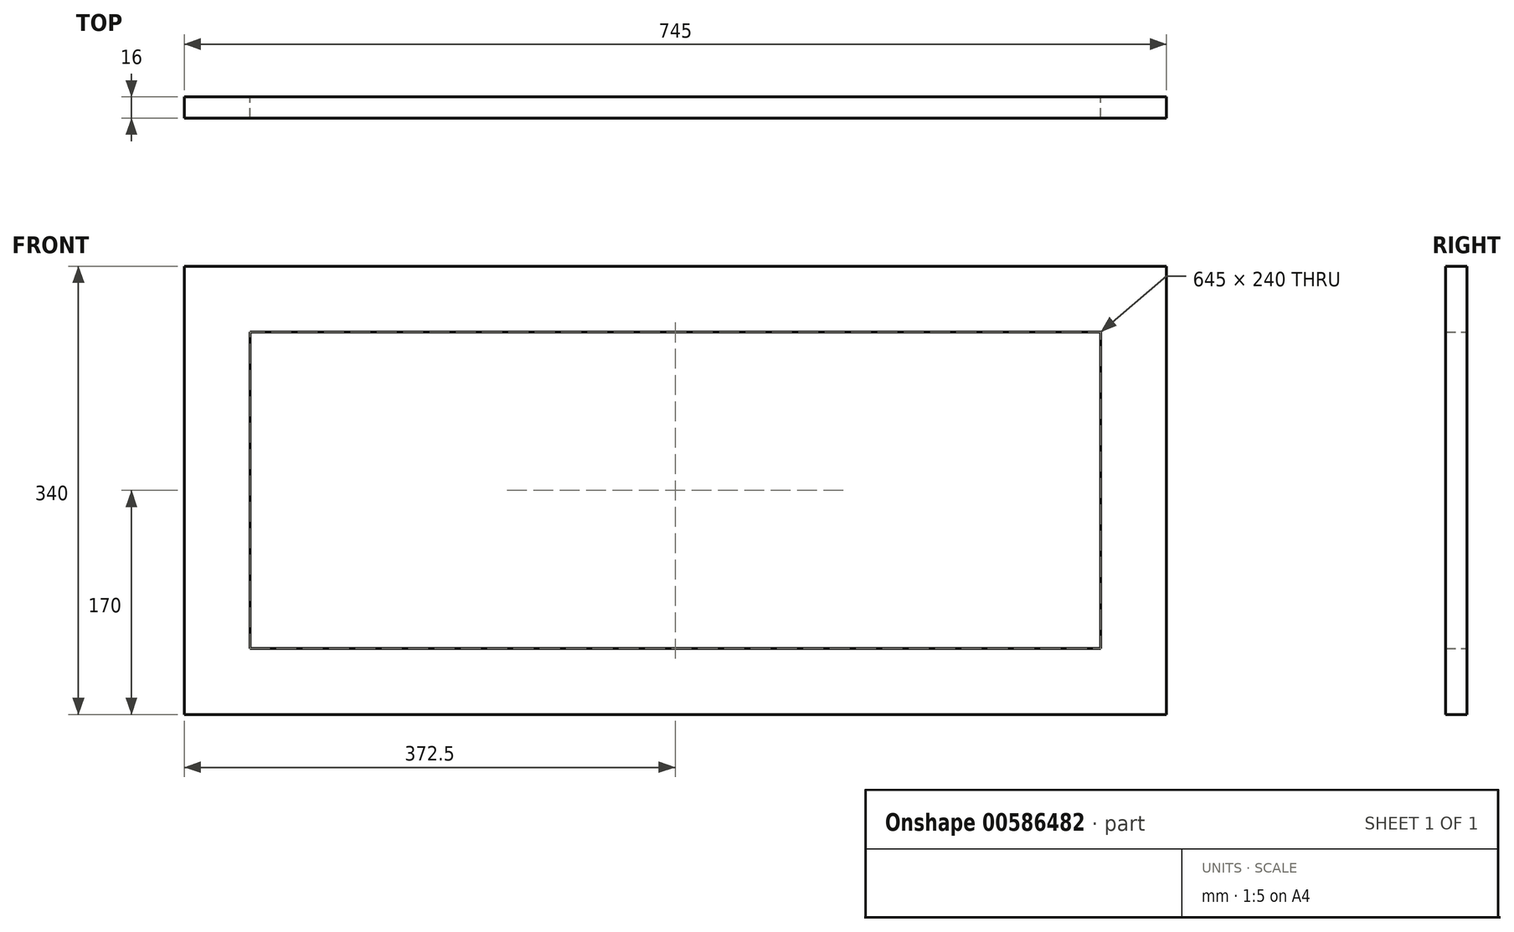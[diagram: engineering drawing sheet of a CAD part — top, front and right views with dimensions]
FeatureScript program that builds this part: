
annotation { "Feature Type Name" : "Feature", "Feature Type Description" : "" }
export const myFeature = defineFeature(function(context is Context, id is Id, definition is map)
    precondition{}
    {
        {
            var Q0;
            Q0=qCreatedBy(makeId("Front.planeOp"),FACE);
            var sketch = newSketch(context, id + "F0", { "sketchPlane" : qUnion([Q0])});
            skLineSegment(sketch, "E0.bottom", {"start": v(-372.5, 170) * mm, "end": v(372.5, 170) * mm});
            skLineSegment(sketch, "E0.top", {"start": v(-372.5, -170) * mm, "end": v(372.5, -170) * mm});
            skLineSegment(sketch, "E0.left", {"start": v(-372.5, 170) * mm, "end": v(-372.5, -170) * mm});
            skLineSegment(sketch, "E0.right", {"start": v(372.5, 170) * mm, "end": v(372.5, -170) * mm});
            skPoint(sketch, "E0.middle", {"position": v(0, 0) * mm});
            skLineSegment(sketch, "E1.0", {"start": v(-322.5, 120) * mm, "end": v(322.5, 120) * mm});
            skLineSegment(sketch, "E2.0", {"start": v(-322.5, 120) * mm, "end": v(-322.5, -120) * mm});
            skLineSegment(sketch, "E3.0", {"start": v(-322.5, -120) * mm, "end": v(322.5, -120) * mm});
            skLineSegment(sketch, "E4.0", {"start": v(322.5, 120) * mm, "end": v(322.5, -120) * mm});
            skSolve(sketch);
        }
        {
            var Q0;
            Q0=makeQuery(id+"F0.imprint","IMPRINT",FACE,{"disambiguationData":[TD([[makeQuery(id+"F0.imprint","IMPRINT",EDGE,{"derivedFrom":sQuery(id+"F0.wireOp",EDGE,"E0.bottom")}),-1.0]])]});
            extrude(context, id + "F1", {"entities" : qUnion([Q0]), "depth" : 16 * mm, "offsetDistance" : 25 * mm});
        }
    });
